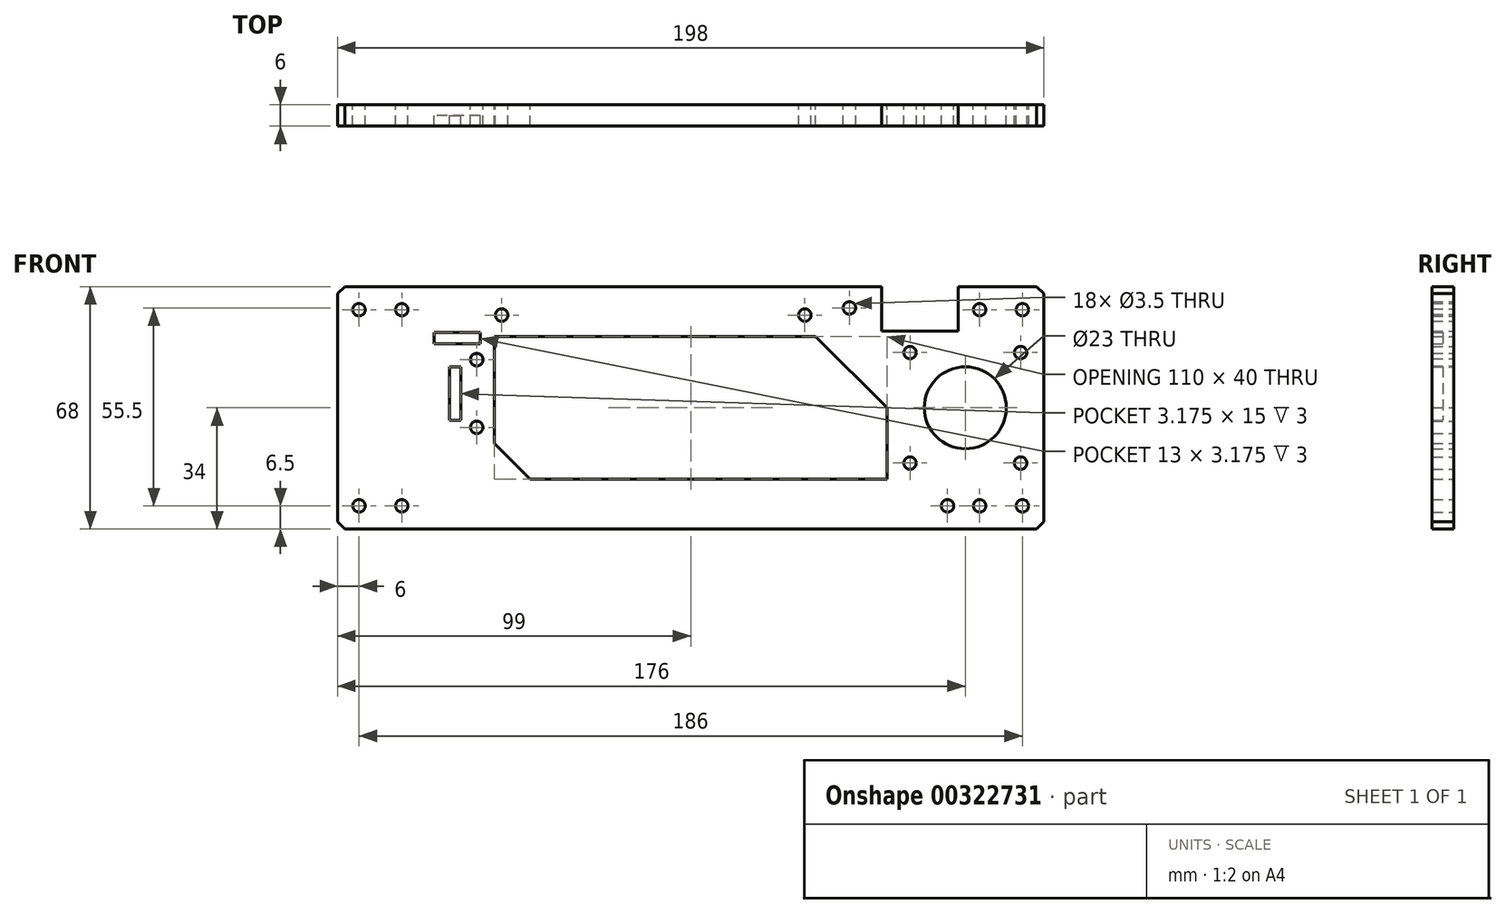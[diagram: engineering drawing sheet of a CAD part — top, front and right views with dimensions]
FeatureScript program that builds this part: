
annotation { "Feature Type Name" : "Feature", "Feature Type Description" : "" }
export const myFeature = defineFeature(function(context is Context, id is Id, definition is map)
    precondition{}
    {
        {
            assignVariable(context, id + "F0", {"name" : "t", "anyValue" : 6});
        }
        {
            var Q0;
            Q0=qCreatedBy(makeId("Front.planeOp"),FACE);
            var sketch = newSketch(context, id + "F1", { "sketchPlane" : qUnion([Q0])});
            skLineSegment(sketch, "E0.bottom", {"start": v(97, 34) * mm, "end": v(75, 34) * mm});
            skLineSegment(sketch, "E0.top", {"start": v(97, -34) * mm, "end": v(-97, -34) * mm});
            skLineSegment(sketch, "E0.left", {"start": v(99, 32) * mm, "end": v(99, -32) * mm});
            skLineSegment(sketch, "E0.right", {"start": v(-99, 32) * mm, "end": v(-99, -32) * mm});
            skPoint(sketch, "E0.middle", {"position": v(0, 0) * mm});
            skCircle(sketch, "E1", {"center": v(-93, 27.5) * mm, "radius": 1.75 * mm});
            skCircle(sketch, "E2", {"center": v(-81, 27.5) * mm, "radius": 1.75 * mm});
            skCircle(sketch, "E3.MirrorC", {"center": v(81, 27.5) * mm, "radius": 1.75 * mm});
            skCircle(sketch, "E4.MirrorC", {"center": v(93, 27.5) * mm, "radius": 1.75 * mm});
            skCircle(sketch, "E5.MirrorC", {"center": v(93, -27.5) * mm, "radius": 1.75 * mm});
            skCircle(sketch, "E6.MirrorC", {"center": v(81, -27.5) * mm, "radius": 1.75 * mm});
            skCircle(sketch, "E7.MirrorC", {"center": v(-81, -27.5) * mm, "radius": 1.75 * mm});
            skCircle(sketch, "E8.MirrorC", {"center": v(-93, -27.5) * mm, "radius": 1.75 * mm});
            skLineSegment(sketch, "E9", {"start": v(-55, 20) * mm, "end": v(-55, -10) * mm});
            skLineSegment(sketch, "E10", {"start": v(-55, -10) * mm, "end": v(-45, -20) * mm});
            skLineSegment(sketch, "E11", {"start": v(-45, -20) * mm, "end": v(55, -20) * mm});
            skLineSegment(sketch, "E12", {"start": v(55, -20) * mm, "end": v(55, 0) * mm});
            skLineSegment(sketch, "E13", {"start": v(55, 0) * mm, "end": v(35, 20) * mm});
            skLineSegment(sketch, "E14", {"start": v(35, 20) * mm, "end": v(-55, 20) * mm});
            skCircle(sketch, "E15", {"center": v(-60, 13.5) * mm, "radius": 1.75 * mm});
            skCircle(sketch, "E16", {"center": v(-60, -5.5) * mm, "radius": 1.75 * mm});
            skLineSegment(sketch, "E17", {"start": v(75, 34) * mm, "end": v(75, 21.5) * mm});
            skLineSegment(sketch, "E18", {"start": v(75, 21.5) * mm, "end": v(53.5, 21.5) * mm});
            skLineSegment(sketch, "E19", {"start": v(53.5, 21.5) * mm, "end": v(53.5, 34) * mm});
            skCircle(sketch, "E20", {"center": v(77, 0) * mm, "radius": 11.5 * mm});
            skCircle(sketch, "E21", {"center": v(92.5, -15.5) * mm, "radius": 1.75 * mm});
            skCircle(sketch, "E22.1.0", {"center": v(92.5, 15.5) * mm, "radius": 1.75 * mm});
            skCircle(sketch, "E22.2.0", {"center": v(61.5, 15.5) * mm, "radius": 1.75 * mm});
            skCircle(sketch, "E22.3.0", {"center": v(61.5, -15.5) * mm, "radius": 1.75 * mm});
            skLineSegment(sketch, "E23", {"start": v(-99, 32) * mm, "end": v(-97, 34) * mm});
            skLineSegment(sketch, "E24.MirrorCS", {"start": v(99, 32) * mm, "end": v(97, 34) * mm});
            skLineSegment(sketch, "E25.MirrorCS", {"start": v(-99, -32) * mm, "end": v(-97, -34) * mm});
            skLineSegment(sketch, "E26.MirrorCS", {"start": v(99, -32) * mm, "end": v(97, -34) * mm});
            skPoint(sketch, "E27.orphan", {"position": v(99, 34) * mm});
            skPoint(sketch, "E28.orphan", {"position": v(99, -34) * mm});
            skPoint(sketch, "E29.orphan", {"position": v(-99, -34) * mm});
            skPoint(sketch, "E30.orphan", {"position": v(-99, 34) * mm});
            skCircle(sketch, "E31.MirrorC", {"center": v(44.5, 28) * mm, "radius": 1.75 * mm});
            skLineSegment(sketch, "E32.trimOffspring", {"start": v(53.5, 34) * mm, "end": v(-97, 34) * mm});
            skLineSegment(sketch, "E33", {"start": v(-60, 13.5) * mm, "end": v(-60, -5.5) * mm, "construction": true});
            skLineSegment(sketch, "E34.bottom", {"start": v(-67.59, 11.5) * mm, "end": v(-64.41, 11.5) * mm});
            skLineSegment(sketch, "E34.top", {"start": v(-67.59, -3.5) * mm, "end": v(-64.41, -3.5) * mm});
            skLineSegment(sketch, "E34.left", {"start": v(-67.59, 11.5) * mm, "end": v(-67.59, -3.5) * mm});
            skLineSegment(sketch, "E34.right", {"start": v(-64.41, 11.5) * mm, "end": v(-64.41, -3.5) * mm});
            skPoint(sketch, "E34.middle", {"position": v(-66, 4) * mm});
            skPoint(sketch, "E34.middle.positionSnap0", {"position": v(-60, 4) * mm});
            skPoint(sketch, "E34.centerSnap0", {"position": v(-60, 4) * mm});
            skLineSegment(sketch, "E35.bottom", {"start": v(-59, 21.09) * mm, "end": v(-72, 21.09) * mm});
            skLineSegment(sketch, "E35.top", {"start": v(-59, 17.91) * mm, "end": v(-72, 17.91) * mm});
            skLineSegment(sketch, "E35.left", {"start": v(-59, 21.09) * mm, "end": v(-59, 17.91) * mm});
            skLineSegment(sketch, "E35.right", {"start": v(-72, 21.09) * mm, "end": v(-72, 17.91) * mm});
            skPoint(sketch, "E35.middle", {"position": v(-65.5, 19.5) * mm});
            skCircle(sketch, "E36", {"center": v(-53, 26) * mm, "radius": 1.75 * mm});
            skCircle(sketch, "E37", {"center": v(32, 26) * mm, "radius": 1.75 * mm});
            skCircle(sketch, "E38", {"center": v(72, -27.5) * mm, "radius": 1.75 * mm});
            skPoint(sketch, "E39", {"position": v(64.25, 21.5) * mm});
            skSolve(sketch);
        }
        {
            var Q0;
            Q0=makeQuery(id+"F1.imprint","IMPRINT",FACE,{"disambiguationData":[TD([[makeQuery(id+"F1.imprint","IMPRINT",EDGE,{"derivedFrom":sQuery(id+"F1.wireOp",EDGE,"E0.top")}),-1.0]])]});
            extrude(context, id + "F2", {"entities" : qUnion([Q0]), "depth" : (getVariable(context, 't')) * mm, "offsetDistance" : 25 * mm});
        }
        {
            var Q0;
            Q0=makeQuery(id+"F1.imprint","IMPRINT",FACE,{"disambiguationData":[TD([[makeQuery(id+"F1.imprint","IMPRINT",EDGE,{"derivedFrom":sQuery(id+"F1.wireOp",EDGE,"E34.bottom")}),-1.0]])]});
            var Q1;
            Q1=makeQuery(id+"F1.imprint","IMPRINT",FACE,{"disambiguationData":[TD([[makeQuery(id+"F1.imprint","IMPRINT",EDGE,{"derivedFrom":sQuery(id+"F1.wireOp",EDGE,"E35.bottom")}),1.0]])]});
            extrude(context, id + "F3", {"entities" : qUnion([Q0, Q1]), "operationType" : NewBodyOperationType.ADD, "depth" : (getVariable(context, 't') - 3) * mm, "offsetDistance" : 25 * mm});
        }
    });
